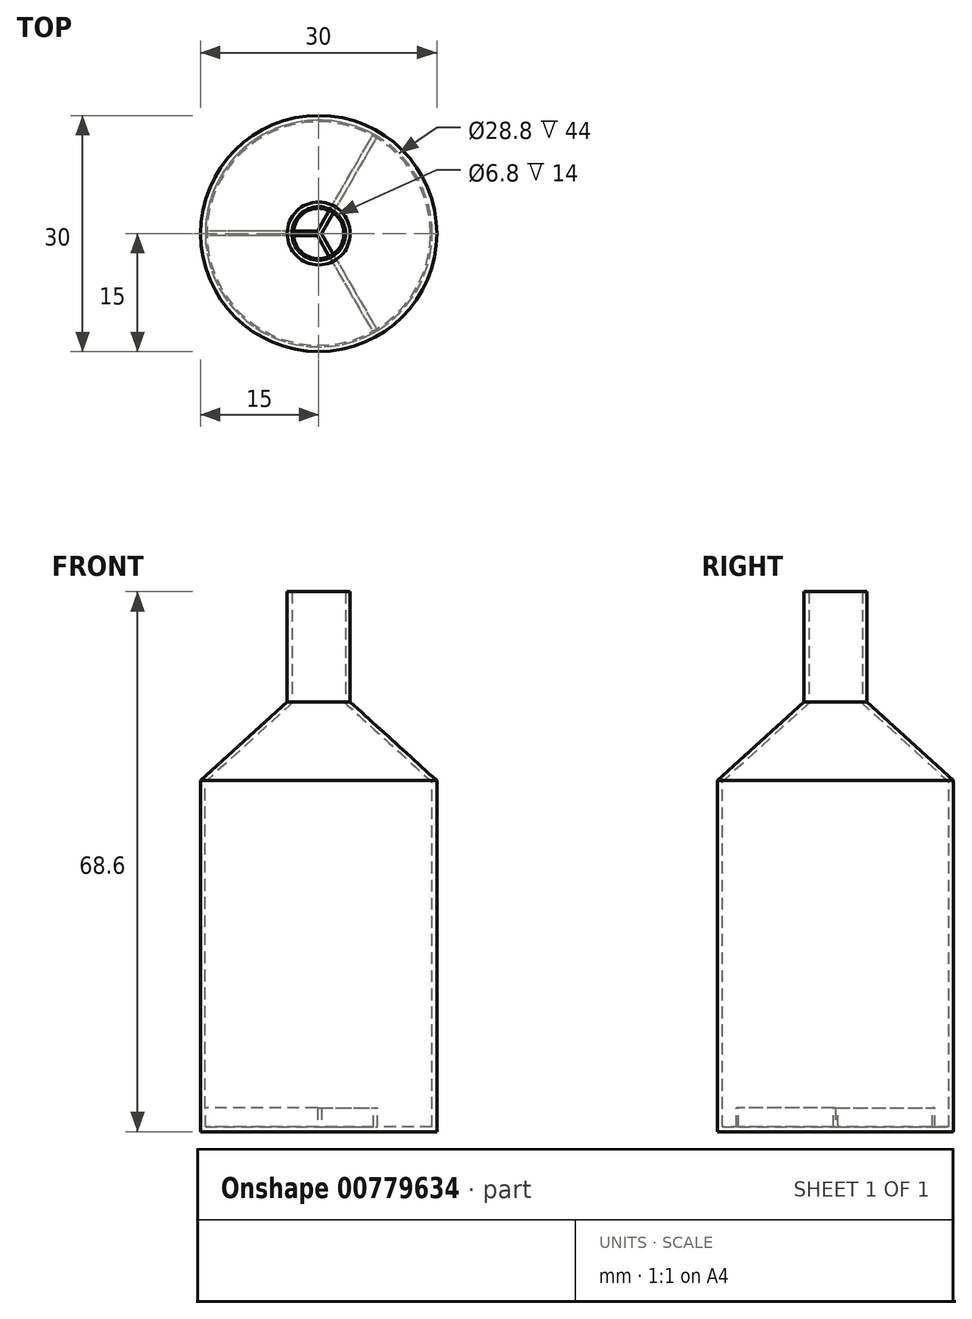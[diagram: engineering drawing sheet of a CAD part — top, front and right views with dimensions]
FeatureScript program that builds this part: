
annotation { "Feature Type Name" : "Feature", "Feature Type Description" : "" }
export const myFeature = defineFeature(function(context is Context, id is Id, definition is map)
    precondition{}
    {
        {
            assignVariable(context, id + "F0", {"name" : "Width", "anyValue" : .6});
        }
        {
            var Q0;
            Q0=qCreatedBy(makeId("Top.planeOp"),FACE);
            cPlane(context, id + "F1", {"entities" : qUnion([Q0]), "cplaneType" : CPlaneType.OFFSET, "offset" : 10 * mm, "oppositeDirection" : true, "width" : 150 * mm, "height" : 150 * mm});
        }
        {
            var Q0;
            Q0=qCreatedBy(makeId("Top.planeOp"),FACE);
            var sketch = newSketch(context, id + "F2", { "sketchPlane" : qUnion([Q0])});
            skCircle(sketch, "E0", {"center": v(0, 0) * mm, "radius": 4 * mm});
            skCircle(sketch, "E1.0", {"center": v(0, 0) * mm, "radius": 3.4 * mm});
            skSolve(sketch);
        }
        {
            var Q0;
            Q0=qCreatedBy(makeId("Top.planeOp"),FACE);
            var sketch = newSketch(context, id + "F3", { "sketchPlane" : qUnion([Q0])});
            skCircle(sketch, "E2.0", {"center": v(0, 0) * mm, "radius": 4 * mm});
            skSolve(sketch);
        }
        {
            var Q0;
            Q0=qCreatedBy(makeId("Top.planeOp"),FACE);
            var sketch = newSketch(context, id + "F4", { "sketchPlane" : qUnion([Q0])});
            skCircle(sketch, "E3.0", {"center": v(0, 0) * mm, "radius": 4 * mm, "construction": true});
            skCircle(sketch, "E4.0", {"center": v(0, 0) * mm, "radius": 3.2 * mm});
            skSolve(sketch);
        }
        {
            var Q0;
            Q0 = qSketchRegion(id + "F2", true);
            extrude(context, id + "F5", {"entities" : qUnion([Q0]), "depth" : 14 * mm, "offsetDistance" : 25 * mm});
        }
        {
            var Q0;
            Q0=qCreatedBy(id+"F1.planeOp",FACE);
            var sketch = newSketch(context, id + "F6", { "sketchPlane" : qUnion([Q0])});
            skCircle(sketch, "E5", {"center": v(0, 0) * mm, "radius": 15 * mm});
            skCircle(sketch, "E6.0", {"center": v(0, 0) * mm, "radius": 14.4 * mm});
            skSolve(sketch);
        }
        {
            var Q0;
            Q0=qCreatedBy(id+"F1.planeOp",FACE);
            var sketch = newSketch(context, id + "F7", { "sketchPlane" : qUnion([Q0])});
            skCircle(sketch, "E7.0", {"center": v(0, 0) * mm, "radius": 15 * mm});
            skSolve(sketch);
        }
        {
            var Q0;
            Q0=qCreatedBy(id+"F1.planeOp",FACE);
            var sketch = newSketch(context, id + "F8", { "sketchPlane" : qUnion([Q0])});
            skCircle(sketch, "E8.0", {"center": v(0, 0) * mm, "radius": 15 * mm, "construction": true});
            skCircle(sketch, "E9.0", {"center": v(0, 0) * mm, "radius": 14.2 * mm});
            skSolve(sketch);
        }
        {
            var Q1;
            Q1 = qSketchRegion(id + "F7", true);
            var Q2;
            Q2 = qSketchRegion(id + "F3", true);
            loft(context, id + "F9", {"operationType" : NewBodyOperationType.ADD, "sheetProfilesArray" : [{ "sheetProfileEntities" : qUnion([Q1]) }, { "sheetProfileEntities" : qUnion([Q2]) }]});
        }
        {
            var Q1;
            Q1 = qSketchRegion(id + "F4", true);
            var Q2;
            Q2 = qSketchRegion(id + "F8", true);
            loft(context, id + "F10", {"operationType" : NewBodyOperationType.REMOVE, "sheetProfilesArray" : [{ "sheetProfileEntities" : qUnion([Q1]) }, { "sheetProfileEntities" : qUnion([Q2]) }]});
        }
        {
            var Q0;
            Q0 = qSketchRegion(id + "F6", true);
            extrude(context, id + "F11", {"entities" : qUnion([Q0]), "operationType" : NewBodyOperationType.ADD, "oppositeDirection" : true, "depth" : 44 * mm, "offsetDistance" : 25 * mm});
        }
        {
            var Q0;
            Q0=makeQuery(id+"F11.opExtrude","CAP_FACE",FACE,{"disambiguationData":[OSD([sQuery(id+"F6.wireOp",EDGE,"E5"),sQuery(id+"F6.wireOp",EDGE,"E6.0")])],"isStart":false});
            cPlane(context, id + "F12", {"entities" : qUnion([Q0]), "cplaneType" : CPlaneType.OFFSET, "offset" : 0 * mm, "width" : 150 * mm, "height" : 150 * mm});
        }
        {
            var Q0;
            Q0=qCreatedBy(id+"F12.planeOp",FACE);
            var sketch = newSketch(context, id + "F13", { "sketchPlane" : qUnion([Q0])});
            skCircle(sketch, "E10.0", {"center": v(0, 0) * mm, "radius": 15 * mm});
            skLineSegment(sketch, "E11", {"start": v(0, 0) * mm, "end": v(-15, 0) * mm, "construction": true});
            skLineSegment(sketch, "E12", {"start": v(0, 0) * mm, "end": v(7.5, -13) * mm, "construction": true});
            skLineSegment(sketch, "E13", {"start": v(0, 0) * mm, "end": v(7.5, 13) * mm, "construction": true});
            skLineSegment(sketch, "E14.0", {"start": v(-0.17, 0.3) * mm, "end": v(-15, 0.3) * mm});
            skLineSegment(sketch, "E14.1", {"start": v(-0.17, 0.3) * mm, "end": v(7.24, 13.14) * mm});
            skLineSegment(sketch, "E15.0", {"start": v(-0.17, -0.3) * mm, "end": v(-15, -0.3) * mm});
            skLineSegment(sketch, "E15.1", {"start": v(-0.17, -0.3) * mm, "end": v(7.24, -13.14) * mm});
            skLineSegment(sketch, "E16.0", {"start": v(0.35, 0) * mm, "end": v(7.76, -12.84) * mm});
            skLineSegment(sketch, "E16.1", {"start": v(0.35, 0) * mm, "end": v(7.76, 12.84) * mm});
            skSolve(sketch);
        }
        {
            var Q0;
            {var subQ0=sQuery(id+"F13.wireOp",EDGE,"E14.0");Q0=makeQuery(id+"F13.imprint","IMPRINT",FACE,{"disambiguationData":[TD([[makeQuery(id+"F13.imprint","IMPRINT",EDGE,{"derivedFrom":subQ0}),1.0]])]});}
            extrude(context, id + "F14", {"entities" : qUnion([Q0]), "operationType" : NewBodyOperationType.ADD, "oppositeDirection" : true, "depth" : (getVariable(context, 'Width') * 4) * mm, "offsetDistance" : 25 * mm});
        }
        {
            var Q0;
            Q0=qCreatedBy(id+"F12.planeOp",FACE);
            var sketch = newSketch(context, id + "F15", { "sketchPlane" : qUnion([Q0])});
            skCircle(sketch, "E17.0", {"center": v(0, 0) * mm, "radius": 15 * mm});
            skSolve(sketch);
        }
        {
            var Q0;
            Q0 = qSketchRegion(id + "F15", true);
            extrude(context, id + "F16", {"entities" : qUnion([Q0]), "operationType" : NewBodyOperationType.ADD, "depth" : (getVariable(context, 'Width')) * mm, "offsetDistance" : 25 * mm});
        }
    });
